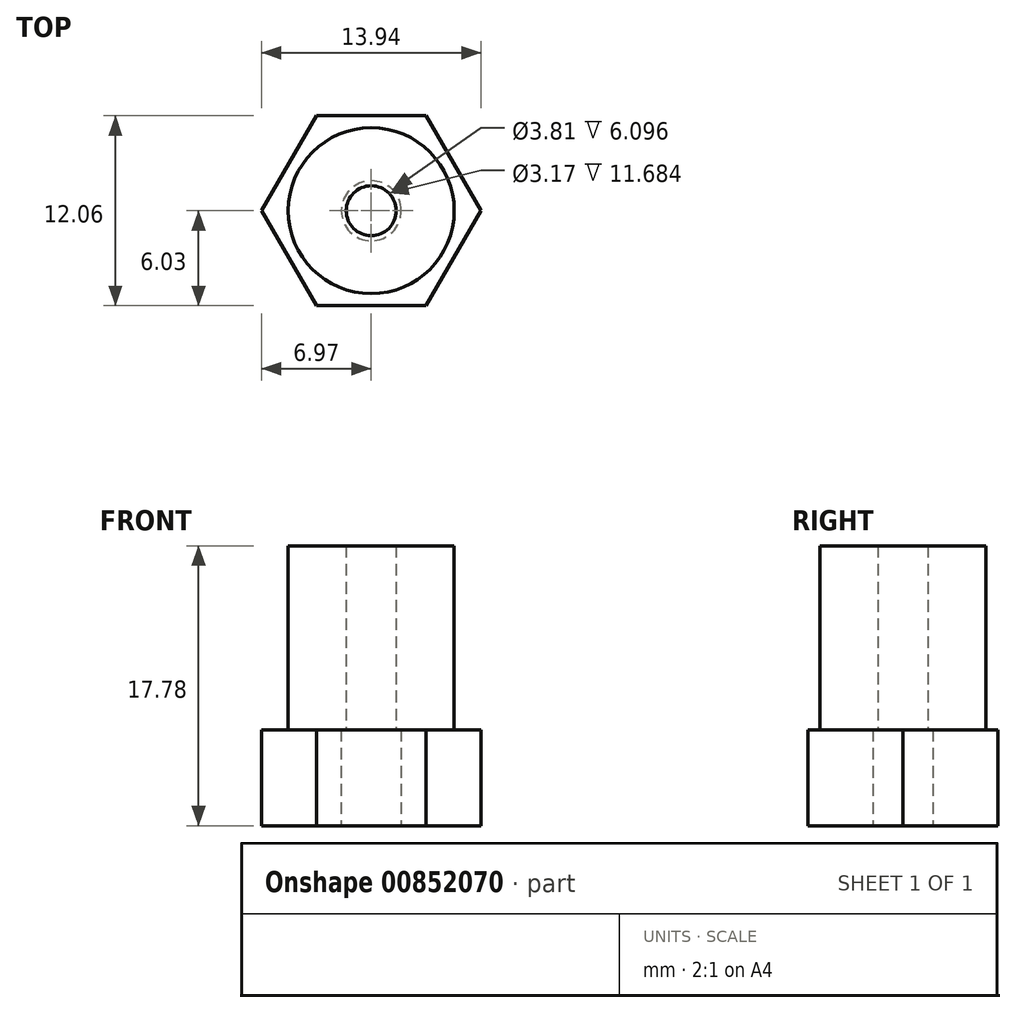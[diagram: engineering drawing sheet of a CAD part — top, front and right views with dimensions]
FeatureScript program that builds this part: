
annotation { "Feature Type Name" : "Feature", "Feature Type Description" : "" }
export const myFeature = defineFeature(function(context is Context, id is Id, definition is map)
    precondition{}
    {
        {
            var Q0;
            Q0=qCreatedBy(makeId("Top.planeOp"),FACE);
            var sketch = newSketch(context, id + "F0", { "sketchPlane" : qUnion([Q0])});
            skCircle(sketch, "E0.cCircle", {"center": v(0, 0) * mm, "radius": 6.03 * mm, "construction": true});
            skLineSegment(sketch, "E0.0", {"start": v(-3.48, 6.03) * mm, "end": v(3.48, 6.03) * mm});
            skLineSegment(sketch, "E0.1", {"start": v(3.48, 6.03) * mm, "end": v(6.97, 0) * mm});
            skLineSegment(sketch, "E0.2", {"start": v(6.97, 0) * mm, "end": v(3.48, -6.03) * mm});
            skLineSegment(sketch, "E0.3", {"start": v(3.48, -6.03) * mm, "end": v(-3.48, -6.03) * mm});
            skLineSegment(sketch, "E0.4", {"start": v(-3.48, -6.03) * mm, "end": v(-6.97, 0) * mm});
            skLineSegment(sketch, "E0.5", {"start": v(-6.97, 0) * mm, "end": v(-3.48, 6.03) * mm});
            skPoint(sketch, "E0.0.midPoint", {"position": v(0, 6.03) * mm});
            skCircle(sketch, "E1", {"center": v(0, 0) * mm, "radius": 1.9 * mm});
            skSolve(sketch);
        }
        {
            var Q0;
            Q0 = qSketchRegion(id + "F0", true);
            extrude(context, id + "F1", {"entities" : qUnion([Q0]), "depth" : 6.1 * mm, "offsetDistance" : 25.4 * mm});
        }
        {
            var Q0;
            Q0=makeQuery(id+"F1.opExtrude","CAP_FACE",FACE,{"disambiguationData":[OSD([sQuery(id+"F0.wireOp",EDGE,"E0.0"),sQuery(id+"F0.wireOp",EDGE,"E0.1"),sQuery(id+"F0.wireOp",EDGE,"E0.2"),sQuery(id+"F0.wireOp",EDGE,"E0.3"),sQuery(id+"F0.wireOp",EDGE,"E0.4"),sQuery(id+"F0.wireOp",EDGE,"E0.5"),sQuery(id+"F0.wireOp",EDGE,"E1")])],"isStart":false});
            var sketch = newSketch(context, id + "F2", { "sketchPlane" : qUnion([Q0])});
            skCircle(sketch, "E2", {"center": v(0, 0) * mm, "radius": 5.27 * mm});
            skCircle(sketch, "E3", {"center": v(0, 0) * mm, "radius": 1.59 * mm});
            skSolve(sketch);
        }
        {
            var Q0;
            Q0 = qSketchRegion(id + "F2", true);
            extrude(context, id + "F3", {"entities" : qUnion([Q0]), "operationType" : NewBodyOperationType.ADD, "depth" : 11.68 * mm, "offsetDistance" : 25.4 * mm});
        }
    });
